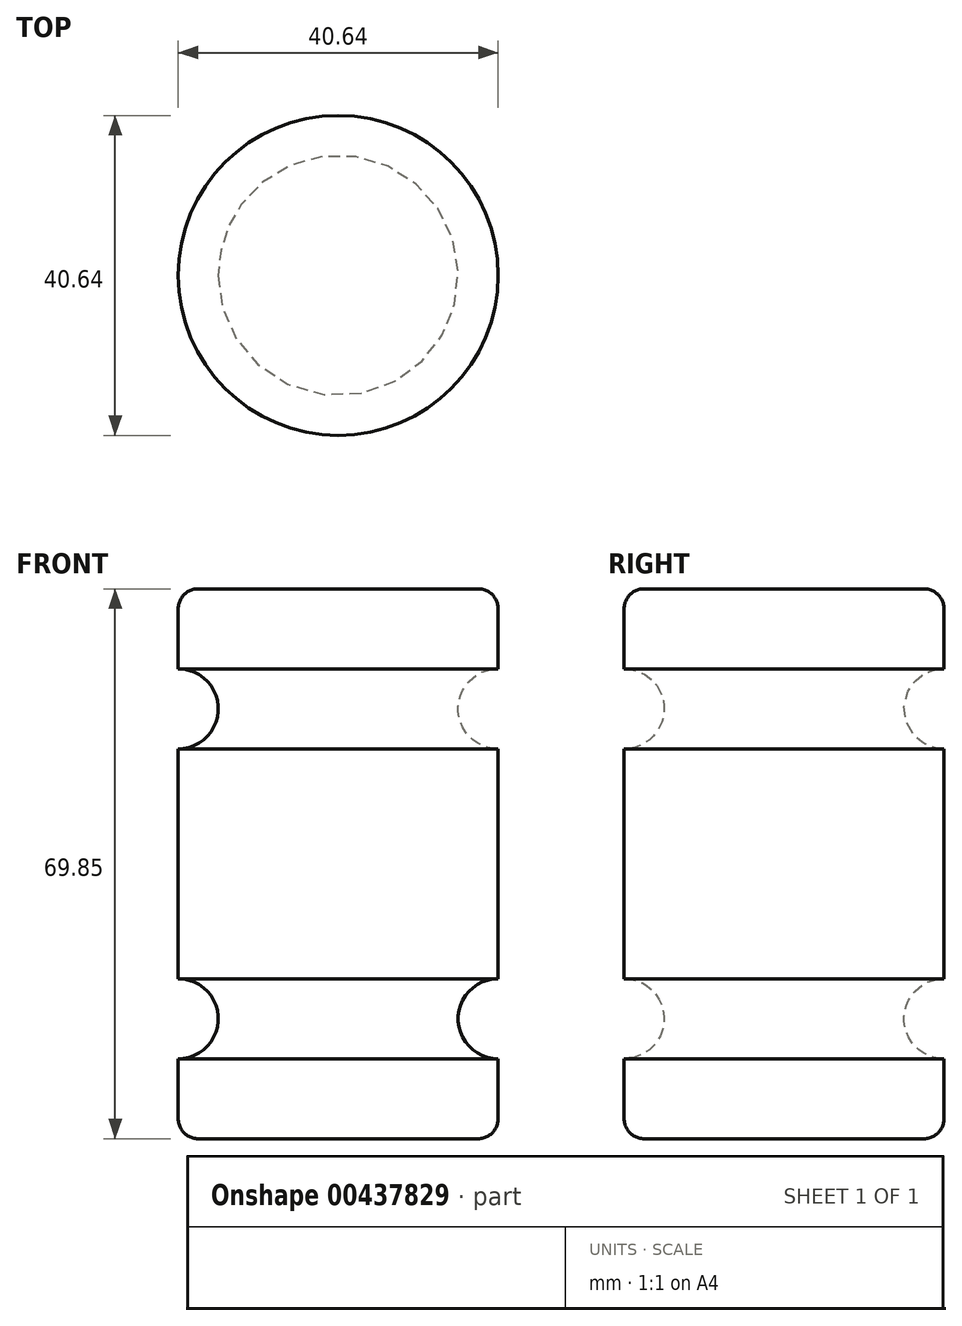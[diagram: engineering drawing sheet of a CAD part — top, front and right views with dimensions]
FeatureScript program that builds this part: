
annotation { "Feature Type Name" : "Feature", "Feature Type Description" : "" }
export const myFeature = defineFeature(function(context is Context, id is Id, definition is map)
    precondition{}
    {
        {
            var Q0;
            Q0=qCreatedBy(makeId("Front.planeOp"),FACE);
            var sketch = newSketch(context, id + "F0", { "sketchPlane" : qUnion([Q0])});
            skLineSegment(sketch, "E0.bottom", {"start": v(0, 0) * mm, "end": v(-20.32, 0) * mm});
            skLineSegment(sketch, "E0.top", {"start": v(0, 69.85) * mm, "end": v(-20.32, 69.85) * mm});
            skLineSegment(sketch, "E0.left", {"start": v(0, 0) * mm, "end": v(0, 10.16) * mm});
            skLineSegment(sketch, "E0.right", {"start": v(-20.32, 0) * mm, "end": v(-20.32, 69.85) * mm});
            skArc(sketch, "E1", {"start": v(0, 59.7) * mm, "mid": v(-5.08, 54.61) * mm, "end": v(0, 49.53) * mm});
            skArc(sketch, "E2", {"start": v(0, 20.32) * mm, "mid": v(-5.08, 15.24) * mm, "end": v(0, 10.16) * mm});
            skLineSegment(sketch, "E3.trimOffspring", {"start": v(0, 59.7) * mm, "end": v(0, 69.85) * mm});
            skLineSegment(sketch, "E4.trimOffspring", {"start": v(0, 20.32) * mm, "end": v(0, 49.53) * mm});
            skSolve(sketch);
        }
        {
            var Q0;
            Q0=makeQuery(id+"F0.imprint","IMPRINT",FACE,{"disambiguationData":[TD([[makeQuery(id+"F0.imprint","IMPRINT",EDGE,{"derivedFrom":sQuery(id+"F0.wireOp",EDGE,"E0.bottom")}),-1.0]])]});
            var Q1;
            Q1=sQuery(id+"F0.wireOp",EDGE,"E0.right");
            revolve(context, id + "F1", {"entities" : qUnion([Q0]), "axis" : qUnion([Q1]), "revolveType" : RevolveType.FULL});
        }
        {
            var Q0;
            Q0=makeQuery(id+"F1.opRevolve","SWEPT_FACE",FACE,{"disambiguationData":[OSD([sQuery(id+"F0.wireOp",EDGE,"E0.top")])]});
            var Q1;
            Q1=makeQuery(id+"F1.opRevolve","SWEPT_FACE",FACE,{"disambiguationData":[OSD([sQuery(id+"F0.wireOp",EDGE,"E0.bottom")])]});
            fillet(context, id + "F2", {"entities" : qUnion([Q0, Q1]), "radius" : 2.54 * mm, "tangentPropagation" : true, "allowEdgeOverflow" : false});
        }
    });
